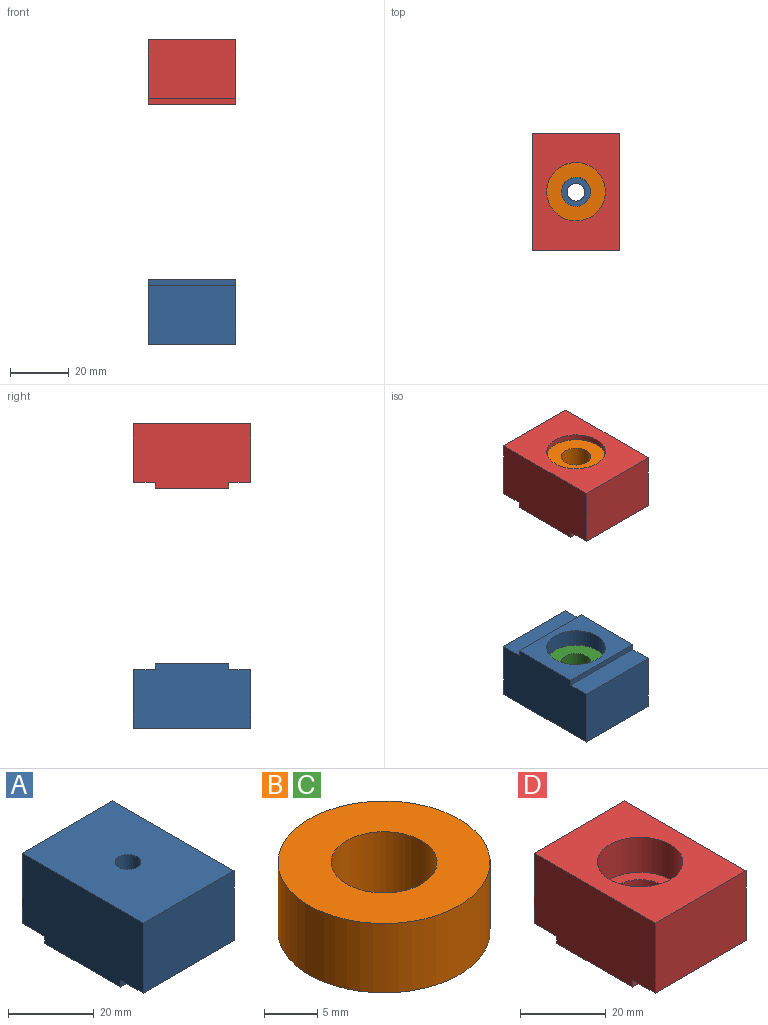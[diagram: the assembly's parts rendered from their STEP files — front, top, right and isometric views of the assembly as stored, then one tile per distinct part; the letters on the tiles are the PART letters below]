
ASSEMBLY  parts=4 mates=3
PART A: 15 faces, bbox 30x40x22 mm
  f0: cylinder r=3mm len=8mm, axis (0,0,-1), area 150.8mm2, adj f6,f13
  f1: plane 30x2mm, normal (0,-1,0), area 60mm2, adj f2,f8,f9,f10
  f2: plane 30x25mm, normal (0,0,-1), area 435.8mm2, adj f1,f3,f9,f10,f11
  f3: plane 30x2mm, normal (0,1,0), area 60mm2, adj f2,f4,f9,f10
  f4: plane 30x7.5mm, normal (0,0,-1), area 225mm2, adj f3,f5,f9,f10
  f5: plane 30x20mm, normal (0,1,0), area 600mm2, adj f4,f6,f9,f10
  f6: plane 40x30mm, normal (0,0,1), area 1171.7mm2, adj f0,f5,f7,f9,f10
  f7: plane 30x20mm, normal (0,-1,0), area 600mm2, adj f6,f8,f9,f10
  f8: plane 30x7.5mm, normal (0,0,-1), area 225mm2, adj f1,f7,f9,f10
  f9: plane 40x22mm, normal (1,0,0), area 850mm2, adj f1,f2,f3,f4,f5,f6,f7,f8
  f10: plane 40x22mm, normal (-1,0,0), area 850mm2, adj f1,f2,f3,f4,f5,f6,f7,f8
  f11: cylinder r=10mm len=20mm, axis (0,0,-1), area 628.3mm2, adj f2,f12
  f12: plane 20x20mm, normal (0,0,-1), area 30.6mm2, adj f11,f14
  f13: plane 19x19mm, normal (0,0,-1), area 255.3mm2, adj f0,f14
  f14: cylinder r=9.5mm len=19mm, axis (0,0,-1), area 238.8mm2, adj f12,f13
PART B: 4 faces, bbox 20x20x8 mm
  f0: cylinder r=5mm len=10mm, axis (0,0,-1), area 251.3mm2, adj f2,f3
  f1: cylinder r=10mm len=20mm, axis (0,0,-1), area 502.7mm2, adj f2,f3
  f2: plane 20x20mm, normal (0,0,1), area 235.6mm2, adj f0,f1
  f3: plane 20x20mm, normal (0,0,-1), area 235.6mm2, adj f0,f1
PART C: same geometry as B
PART D: 13 faces, bbox 30x40x22 mm
  f0: cylinder r=7mm len=14mm, axis (0,0,-1), area 527.8mm2, adj f2,f12
  f1: plane 30x2mm, normal (0,-1,0), area 60mm2, adj f2,f8,f9,f10
  f2: plane 30x25mm, normal (0,0,-1), area 596.1mm2, adj f0,f1,f3,f9,f10
  f3: plane 30x2mm, normal (0,1,0), area 60mm2, adj f2,f4,f9,f10
  f4: plane 30x7.5mm, normal (0,0,-1), area 225mm2, adj f3,f5,f9,f10
  f5: plane 30x20mm, normal (0,1,0), area 600mm2, adj f4,f6,f9,f10
  f6: plane 40x30mm, normal (0,0,1), area 885.8mm2, adj f5,f7,f9,f10,f11
  f7: plane 30x20mm, normal (0,-1,0), area 600mm2, adj f6,f8,f9,f10
  f8: plane 30x7.5mm, normal (0,0,-1), area 225mm2, adj f1,f7,f9,f10
  f9: plane 40x22mm, normal (1,0,0), area 850mm2, adj f1,f2,f3,f4,f5,f6,f7,f8
  f10: plane 40x22mm, normal (-1,0,0), area 850mm2, adj f1,f2,f3,f4,f5,f6,f7,f8
  f11: cylinder r=10mm len=20mm, axis (0,0,1), area 628.3mm2, adj f6,f12
  f12: plane 20x20mm, normal (0,0,1), area 160.2mm2, adj f0,f11
PLACE A rot(axis=(1,0,0),180deg) t=(-15,0,-62)mm
PLACE B t=(0,0,12)mm
PLACE C t=(0,0,-74)mm
PLACE D t=(-15,0,2)mm
MATE fastened A.f0 <-> C.f0  axis (0,0,1) through (0,0,-74)mm
MATE revolute B.f0 <-> D.f0  axis (0,0,-1) through (0,0,12)mm
MATE fastened A.f11 <-> D.f0  axis (0,0,1) through (0,0,-60)mm
